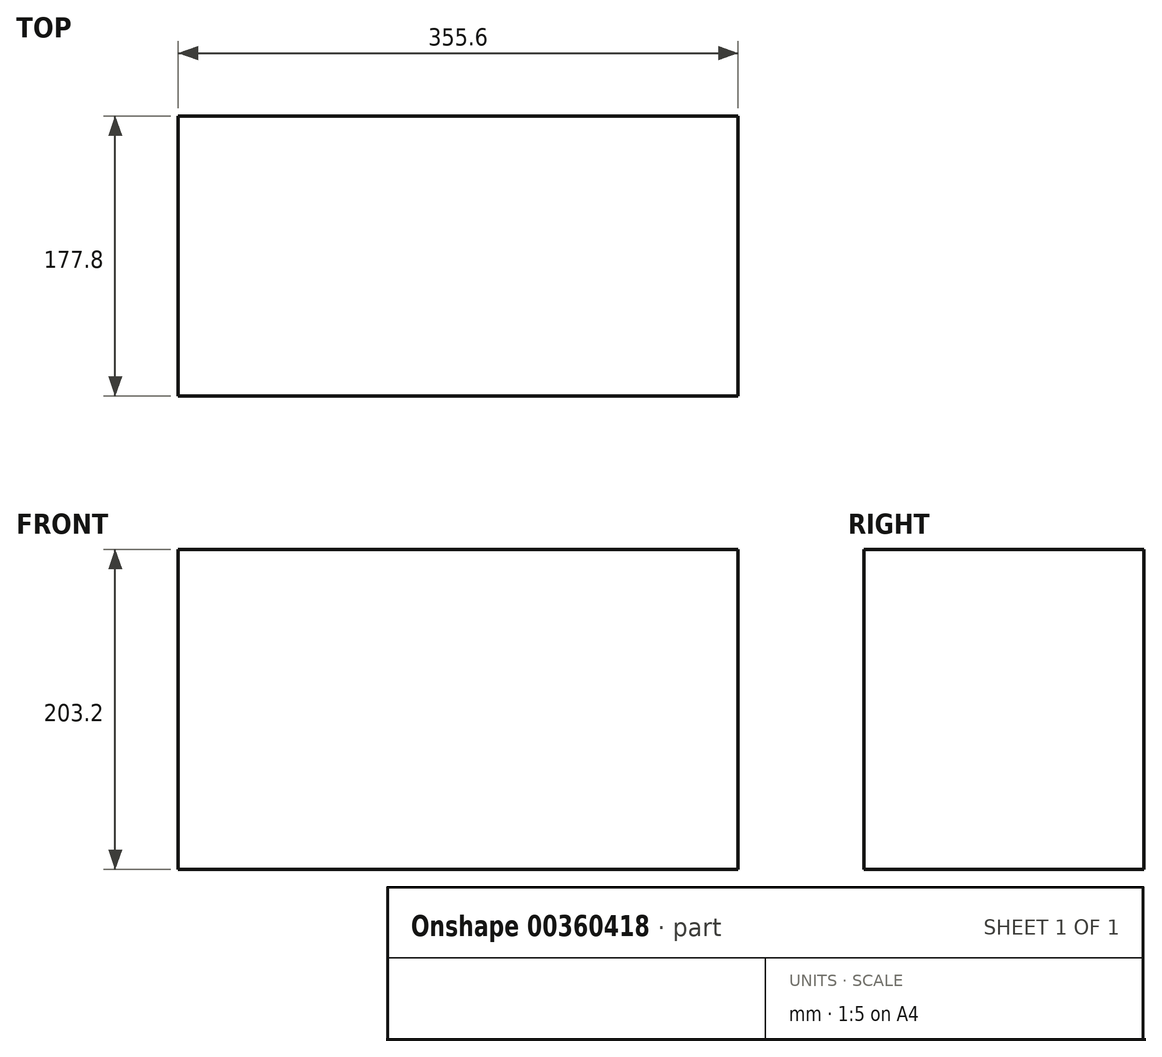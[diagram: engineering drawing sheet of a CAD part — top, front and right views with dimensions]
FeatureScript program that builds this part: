
annotation { "Feature Type Name" : "Feature", "Feature Type Description" : "" }
export const myFeature = defineFeature(function(context is Context, id is Id, definition is map)
    precondition{}
    {
        {
            var Q0;
            Q0=qCreatedBy(makeId("Top.planeOp"),FACE);
            var sketch = newSketch(context, id + "F0", { "sketchPlane" : qUnion([Q0])});
            skLineSegment(sketch, "E0.bottom", {"start": v(177.8, 88.9) * mm, "end": v(-177.8, 88.9) * mm});
            skLineSegment(sketch, "E0.top", {"start": v(177.8, -88.9) * mm, "end": v(-177.8, -88.9) * mm});
            skLineSegment(sketch, "E0.left", {"start": v(177.8, 88.9) * mm, "end": v(177.8, -88.9) * mm});
            skLineSegment(sketch, "E0.right", {"start": v(-177.8, 88.9) * mm, "end": v(-177.8, -88.9) * mm});
            skPoint(sketch, "E0.middle", {"position": v(0, 0) * mm});
            skSolve(sketch);
        }
        {
            var Q0;
            Q0=makeQuery(id+"F0.imprint","IMPRINT",FACE,{"disambiguationData":[TD([[makeQuery(id+"F0.imprint","IMPRINT",EDGE,{"derivedFrom":sQuery(id+"F0.wireOp",EDGE,"E0.bottom")}),1.0]])]});
            extrude(context, id + "F1", {"entities" : qUnion([Q0]), "endBound" : BoundingType.SYMMETRIC, "depth" : 203.2 * mm});
        }
    });
